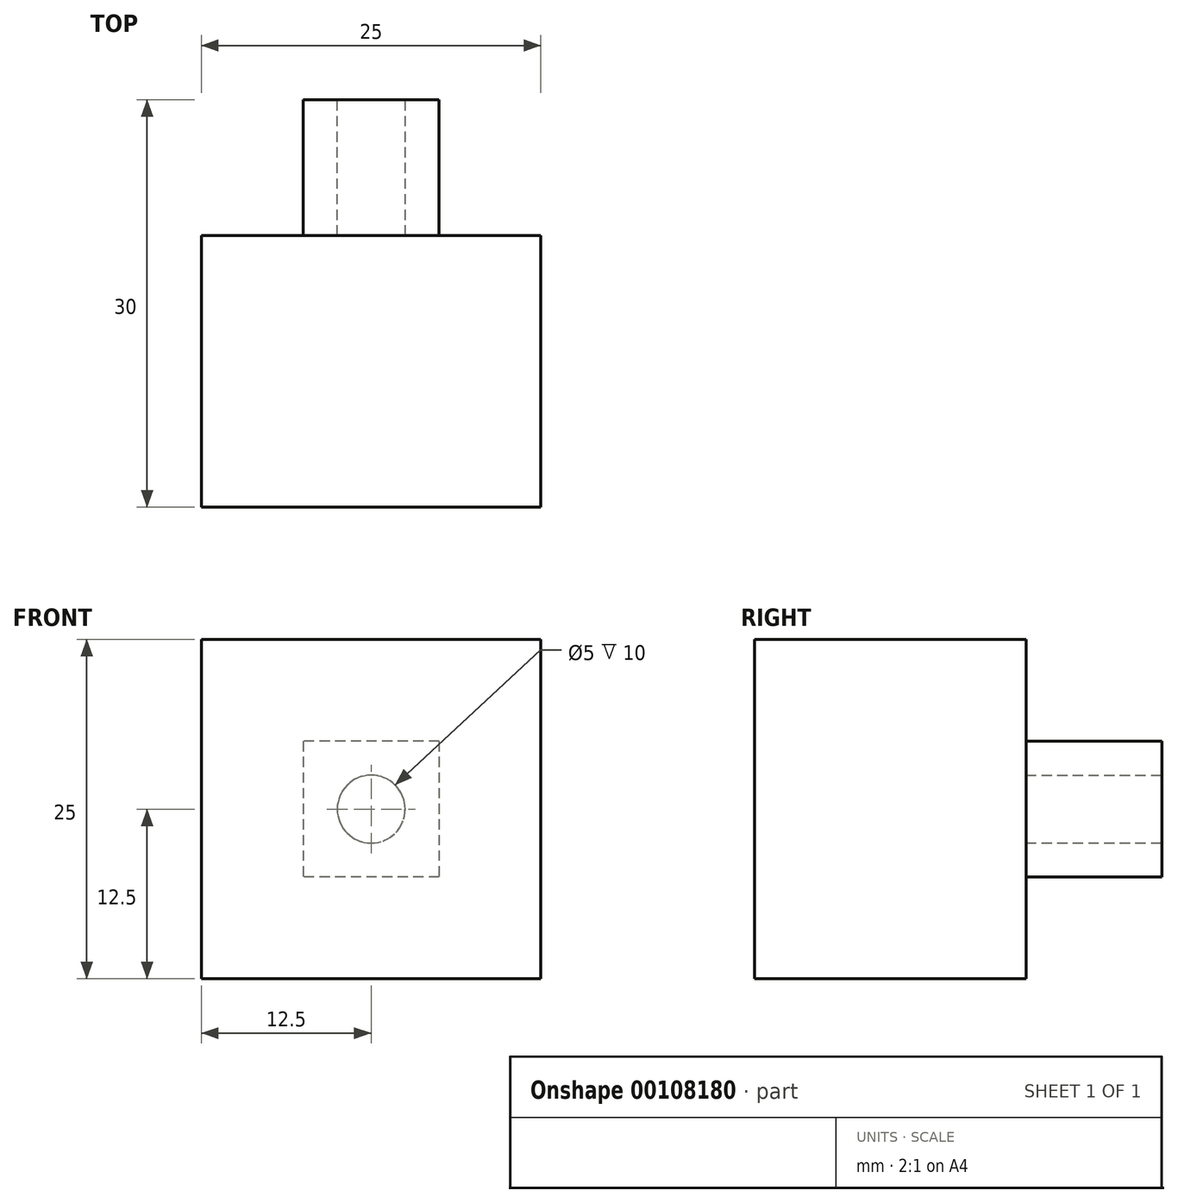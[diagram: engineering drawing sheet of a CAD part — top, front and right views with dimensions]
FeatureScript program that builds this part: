
annotation { "Feature Type Name" : "Feature", "Feature Type Description" : "" }
export const myFeature = defineFeature(function(context is Context, id is Id, definition is map)
    precondition{}
    {
        {
            var Q0;
            Q0=qCreatedBy(makeId("Top.planeOp"),FACE);
            var sketch = newSketch(context, id + "F0", { "sketchPlane" : qUnion([Q0])});
            skLineSegment(sketch, "E0.bottom", {"start": v(12.5, -10) * mm, "end": v(-12.5, -10) * mm});
            skLineSegment(sketch, "E0.top", {"start": v(12.5, 10) * mm, "end": v(-12.5, 10) * mm});
            skLineSegment(sketch, "E0.left", {"start": v(12.5, -10) * mm, "end": v(12.5, 10) * mm});
            skLineSegment(sketch, "E0.right", {"start": v(-12.5, -10) * mm, "end": v(-12.5, 10) * mm});
            skPoint(sketch, "E0.middle", {"position": v(0, 0) * mm});
            skSolve(sketch);
        }
        {
            var Q0;
            Q0=makeQuery(id+"F0.imprint","IMPRINT",FACE,{"disambiguationData":[TD([[makeQuery(id+"F0.imprint","IMPRINT",EDGE,{"derivedFrom":sQuery(id+"F0.wireOp",EDGE,"E0.bottom")}),-1.0]])]});
            extrude(context, id + "F1", {"entities" : qUnion([Q0]), "depth" : 25 * mm});
        }
        {
            var Q0;
            Q0=makeQuery(id+"F1.opExtrude","SWEPT_FACE",FACE,{"disambiguationData":[OSD([sQuery(id+"F0.wireOp",EDGE,"E0.top")])]});
            var sketch = newSketch(context, id + "F2", { "sketchPlane" : qUnion([Q0])});
            skLineSegment(sketch, "E1.bottom", {"start": v(-5, 17.5) * mm, "end": v(5, 17.5) * mm});
            skLineSegment(sketch, "E1.top", {"start": v(-5, 7.5) * mm, "end": v(5, 7.5) * mm});
            skLineSegment(sketch, "E1.left", {"start": v(-5, 17.5) * mm, "end": v(-5, 7.5) * mm});
            skLineSegment(sketch, "E1.right", {"start": v(5, 17.5) * mm, "end": v(5, 7.5) * mm});
            skPoint(sketch, "E1.middle", {"position": v(0, 12.5) * mm});
            skLineSegment(sketch, "E2", {"start": v(0, 25) * mm, "end": v(0, 0) * mm, "construction": true});
            skSolve(sketch);
        }
        {
            var Q0;
            Q0 = qSketchRegion(id + "F2", true);
            extrude(context, id + "F3", {"entities" : qUnion([Q0]), "operationType" : NewBodyOperationType.ADD, "depth" : 10 * mm});
        }
        {
            var Q0;
            Q0=makeQuery(id+"F3.opExtrude","CAP_FACE",FACE,{"disambiguationData":[OSD([sQuery(id+"F2.wireOp",EDGE,"E1.bottom"),sQuery(id+"F2.wireOp",EDGE,"E1.top"),sQuery(id+"F2.wireOp",EDGE,"E1.left"),sQuery(id+"F2.wireOp",EDGE,"E1.right")])],"isStart":false});
            var sketch = newSketch(context, id + "F4", { "sketchPlane" : qUnion([Q0])});
            skCircle(sketch, "E3", {"center": v(0, 12.5) * mm, "radius": 2.5 * mm});
            skPoint(sketch, "E3.centerSnap0", {"position": v(-5, 12.5) * mm});
            skSolve(sketch);
        }
        {
            var Q0;
            Q0 = qSketchRegion(id + "F4", true);
            var Q1;
            Q1=makeQuery(id+"F1.opExtrude","SWEPT_FACE",FACE,{"disambiguationData":[OSD([sQuery(id+"F0.wireOp",EDGE,"E0.top")])]});
            extrude(context, id + "F5", {"entities" : qUnion([Q0]), "operationType" : NewBodyOperationType.REMOVE, "endBound" : BoundingType.UP_TO_SURFACE, "oppositeDirection" : true, "endBoundEntityFace" : qUnion([Q1]), "depth" : 25 * mm});
        }
    });
